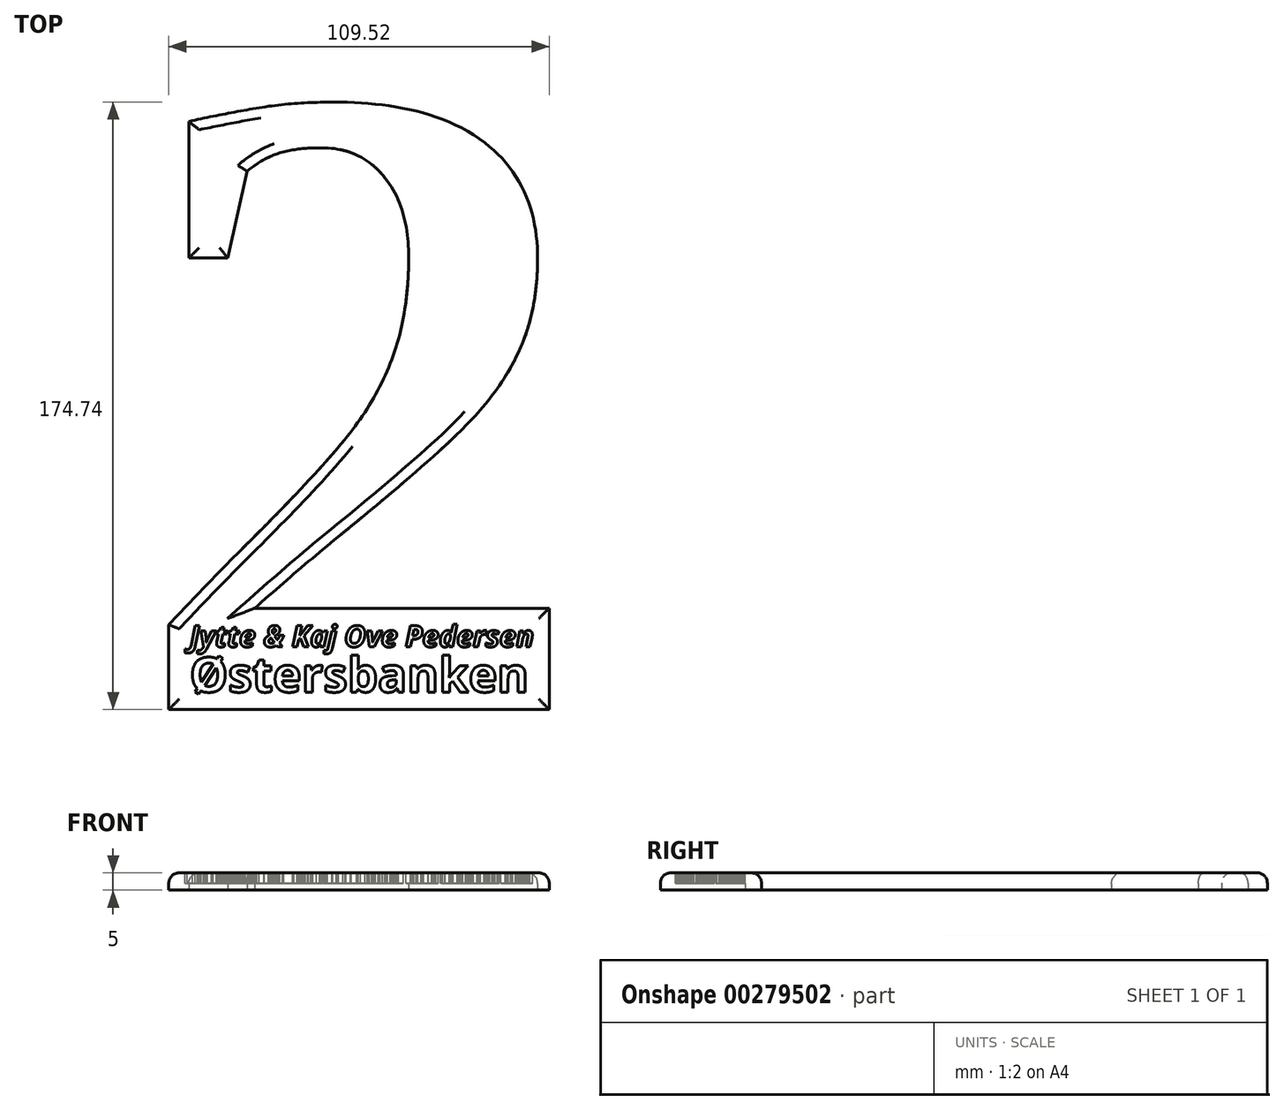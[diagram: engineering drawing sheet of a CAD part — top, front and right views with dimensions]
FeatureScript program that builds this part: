
annotation { "Feature Type Name" : "Feature", "Feature Type Description" : "" }
export const myFeature = defineFeature(function(context is Context, id is Id, definition is map)
    precondition{}
    {
        {
            var Q0;
            Q0=qCreatedBy(makeId("Top.planeOp"),FACE);
            var sketch = newSketch(context, id + "F0", { "sketchPlane" : qUnion([Q0])});
            skText(sketch, "E0", { "text": "2", "fontName": "Tinos-Bold.ttf"});
            const initialGuessF0  = {"E0": [-0.06855, -0.095, 1, 0, 0.19]};
            skSetInitialGuess(sketch, initialGuessF0);
            skSolve(sketch);
        }
        {
            var Q0;
            Q0=makeQuery(id+"F0.imprint","IMPRINT",FACE,{"disambiguationData":[TD([[makeQuery(id+"F0.imprint","IMPRINT",EDGE,{"derivedFrom":sQuery(id+"F0.wireOp",EDGE,"E0.sketch_text.stroke-0")}),-1.0]])]});
            extrude(context, id + "F1", {"entities" : qUnion([Q0]), "depth" : 5 * mm});
        }
        {
            var Q0;
            Q0=makeQuery(id+"F1.opExtrude","CAP_FACE",FACE,{"disambiguationData":[OSD([sQuery(id+"F0.wireOp",EDGE,"E0.sketch_text.stroke-0"),sQuery(id+"F0.wireOp",EDGE,"E0.sketch_text.stroke-1"),sQuery(id+"F0.wireOp",EDGE,"E0.sketch_text.stroke-2"),sQuery(id+"F0.wireOp",EDGE,"E0.sketch_text.stroke-3"),sQuery(id+"F0.wireOp",EDGE,"E0.sketch_text.stroke-4"),sQuery(id+"F0.wireOp",EDGE,"E0.sketch_text.stroke-5"),sQuery(id+"F0.wireOp",EDGE,"E0.sketch_text.stroke-6"),sQuery(id+"F0.wireOp",EDGE,"E0.sketch_text.stroke-7"),sQuery(id+"F0.wireOp",EDGE,"E0.sketch_text.stroke-8"),sQuery(id+"F0.wireOp",EDGE,"E0.sketch_text.stroke-9"),sQuery(id+"F0.wireOp",EDGE,"E0.sketch_text.stroke-10"),sQuery(id+"F0.wireOp",EDGE,"E0.sketch_text.stroke-11"),sQuery(id+"F0.wireOp",EDGE,"E0.sketch_text.stroke-12"),sQuery(id+"F0.wireOp",EDGE,"E0.sketch_text.stroke-13"),sQuery(id+"F0.wireOp",EDGE,"E0.sketch_text.stroke-14"),sQuery(id+"F0.wireOp",EDGE,"E0.sketch_text.stroke-15"),sQuery(id+"F0.wireOp",EDGE,"E0.sketch_text.stroke-16"),sQuery(id+"F0.wireOp",EDGE,"E0.sketch_text.stroke-17"),sQuery(id+"F0.wireOp",EDGE,"E0.sketch_text.stroke-18"),sQuery(id+"F0.wireOp",EDGE,"E0.sketch_text.stroke-19"),sQuery(id+"F0.wireOp",EDGE,"E0.sketch_text.stroke-20"),sQuery(id+"F0.wireOp",EDGE,"E0.sketch_text.stroke-21"),sQuery(id+"F0.wireOp",EDGE,"E0.sketch_text.stroke-22")])],"isStart":false});
            fillet(context, id + "F2", {"entities" : qUnion([Q0]), "radius" : 3 * mm, "tangentPropagation" : true, "allowEdgeOverflow" : false});
        }
        {
            var Q0;
            Q0=makeQuery(id+"F1.opExtrude","CAP_FACE",FACE,{"disambiguationData":[OSD([sQuery(id+"F0.wireOp",EDGE,"E0.sketch_text.stroke-0"),sQuery(id+"F0.wireOp",EDGE,"E0.sketch_text.stroke-1"),sQuery(id+"F0.wireOp",EDGE,"E0.sketch_text.stroke-2"),sQuery(id+"F0.wireOp",EDGE,"E0.sketch_text.stroke-3"),sQuery(id+"F0.wireOp",EDGE,"E0.sketch_text.stroke-4"),sQuery(id+"F0.wireOp",EDGE,"E0.sketch_text.stroke-5"),sQuery(id+"F0.wireOp",EDGE,"E0.sketch_text.stroke-6"),sQuery(id+"F0.wireOp",EDGE,"E0.sketch_text.stroke-7"),sQuery(id+"F0.wireOp",EDGE,"E0.sketch_text.stroke-8"),sQuery(id+"F0.wireOp",EDGE,"E0.sketch_text.stroke-9"),sQuery(id+"F0.wireOp",EDGE,"E0.sketch_text.stroke-10"),sQuery(id+"F0.wireOp",EDGE,"E0.sketch_text.stroke-11"),sQuery(id+"F0.wireOp",EDGE,"E0.sketch_text.stroke-12"),sQuery(id+"F0.wireOp",EDGE,"E0.sketch_text.stroke-13"),sQuery(id+"F0.wireOp",EDGE,"E0.sketch_text.stroke-14"),sQuery(id+"F0.wireOp",EDGE,"E0.sketch_text.stroke-15"),sQuery(id+"F0.wireOp",EDGE,"E0.sketch_text.stroke-16"),sQuery(id+"F0.wireOp",EDGE,"E0.sketch_text.stroke-17"),sQuery(id+"F0.wireOp",EDGE,"E0.sketch_text.stroke-18"),sQuery(id+"F0.wireOp",EDGE,"E0.sketch_text.stroke-19"),sQuery(id+"F0.wireOp",EDGE,"E0.sketch_text.stroke-20"),sQuery(id+"F0.wireOp",EDGE,"E0.sketch_text.stroke-21"),sQuery(id+"F0.wireOp",EDGE,"E0.sketch_text.stroke-22")])],"isStart":false});
            var sketch = newSketch(context, id + "F3", { "sketchPlane" : qUnion([Q0])});
            skText(sketch, "E1", { "text": "Østersbanken", "fontName": "OpenSans-Bold.ttf"});
            skText(sketch, "E2", { "text": "Jytte & Kaj Ove Pedersen", "fontName": "OpenSans-BoldItalic.ttf"});
            const initialGuessF3  = {"E1": [-0.05146, -0.09, 1, 0, 0.01], "E2": [-0.05146, -0.077, 1, 0, 0.00614]};
            skSetInitialGuess(sketch, initialGuessF3);
            skSolve(sketch);
        }
        {
            var Q0;
            Q0 = qSketchRegion(id + "F3", true);
            extrude(context, id + "F4", {"entities" : qUnion([Q0]), "operationType" : NewBodyOperationType.REMOVE, "oppositeDirection" : true, "depth" : 3 * mm});
        }
    });
